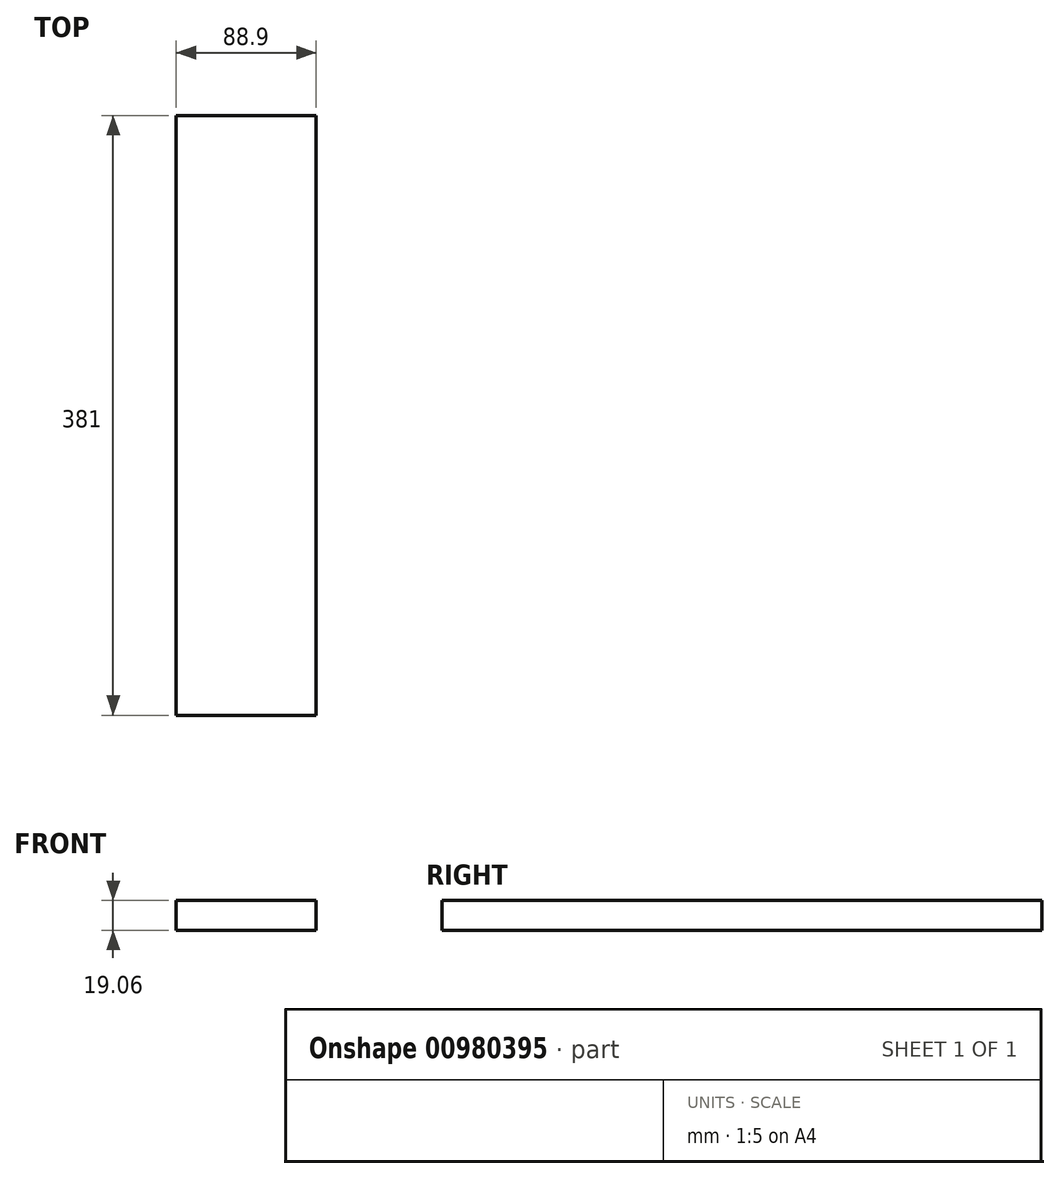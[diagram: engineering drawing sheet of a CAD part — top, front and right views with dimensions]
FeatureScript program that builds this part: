
annotation { "Feature Type Name" : "Feature", "Feature Type Description" : "" }
export const myFeature = defineFeature(function(context is Context, id is Id, definition is map)
    precondition{}
    {
        {
            var Q0;
            Q0=qCreatedBy(makeId("Front.planeOp"),FACE);
            var sketch = newSketch(context, id + "F0", { "sketchPlane" : qUnion([Q0])});
            skLineSegment(sketch, "E0.bottom", {"start": v(44.45, -9.52) * mm, "end": v(-44.45, -9.53) * mm});
            skLineSegment(sketch, "E0.top", {"start": v(44.45, 9.53) * mm, "end": v(-44.45, 9.53) * mm});
            skLineSegment(sketch, "E0.left", {"start": v(44.45, -9.52) * mm, "end": v(44.45, 9.53) * mm});
            skLineSegment(sketch, "E0.right", {"start": v(-44.45, -9.53) * mm, "end": v(-44.45, 9.53) * mm});
            skPoint(sketch, "E0.middle", {"position": v(0, 0) * mm});
            skSolve(sketch);
        }
        {
            var Q0;
            Q0 = qSketchRegion(id + "F0", true);
            extrude(context, id + "F1", {"entities" : qUnion([Q0]), "endBound" : BoundingType.SYMMETRIC, "depth" : 381 * mm, "offsetDistance" : 25.4 * mm});
        }
    });
